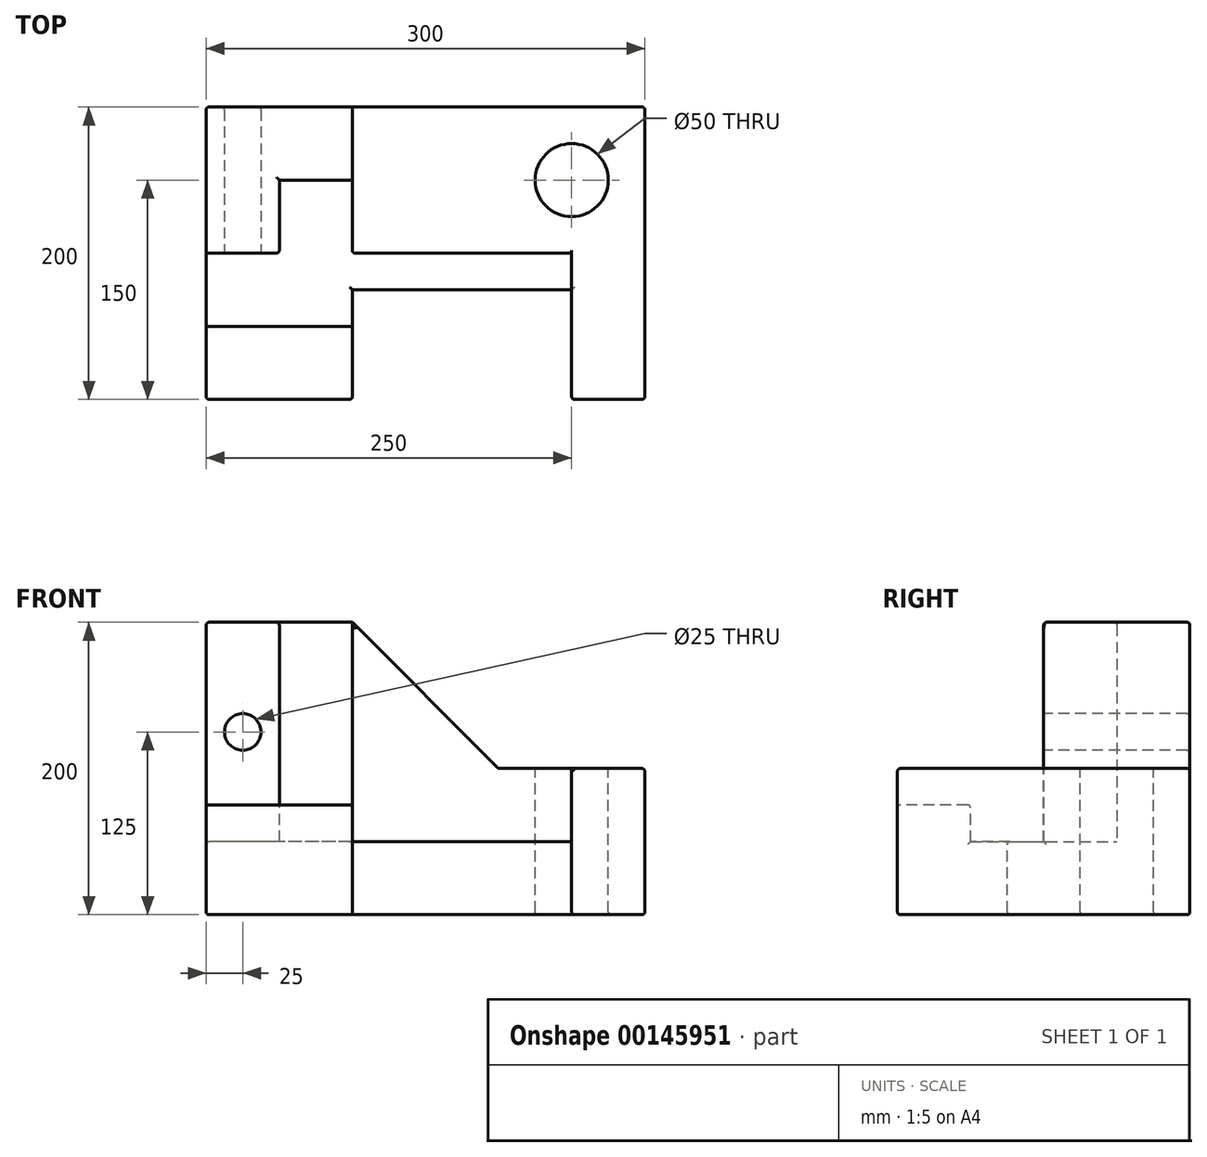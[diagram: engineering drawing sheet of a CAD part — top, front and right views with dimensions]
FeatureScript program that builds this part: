
annotation { "Feature Type Name" : "Feature", "Feature Type Description" : "" }
export const myFeature = defineFeature(function(context is Context, id is Id, definition is map)
    precondition{}
    {
        {
            var Q0;
            Q0=qCreatedBy(makeId("Front.planeOp"),FACE);
            var sketch = newSketch(context, id + "F0", { "sketchPlane" : qUnion([Q0])});
            skLineSegment(sketch, "E0", {"start": v(0, 0) * mm, "end": v(0, 200) * mm});
            skLineSegment(sketch, "E1", {"start": v(0, 200) * mm, "end": v(100, 200) * mm});
            skLineSegment(sketch, "E2", {"start": v(200, 50) * mm, "end": v(250, 50) * mm});
            skLineSegment(sketch, "E3", {"start": v(300, 50) * mm, "end": v(300, 0) * mm});
            skLineSegment(sketch, "E4", {"start": v(300, 0) * mm, "end": v(0, 0) * mm});
            skLineSegment(sketch, "E5", {"start": v(100, 200) * mm, "end": v(100, 50) * mm});
            skLineSegment(sketch, "E6", {"start": v(100, 50) * mm, "end": v(0, 50) * mm});
            skLineSegment(sketch, "E7", {"start": v(100, 50) * mm, "end": v(200, 50) * mm});
            skLineSegment(sketch, "E8", {"start": v(250, 50) * mm, "end": v(250, 0) * mm});
            skLineSegment(sketch, "E9", {"start": v(50, 50) * mm, "end": v(50, 200) * mm});
            skLineSegment(sketch, "E10", {"start": v(200, 100) * mm, "end": v(250, 100) * mm});
            skLineSegment(sketch, "E11", {"start": v(250, 50) * mm, "end": v(250, 100) * mm});
            skLineSegment(sketch, "E12", {"start": v(300, 50) * mm, "end": v(300, 100) * mm});
            skLineSegment(sketch, "E13", {"start": v(300, 100) * mm, "end": v(250, 100) * mm});
            skLineSegment(sketch, "E14", {"start": v(100, 200) * mm, "end": v(200, 100) * mm});
            skPoint(sketch, "E15.orphan", {"position": v(150, 200) * mm});
            skSolve(sketch);
        }
        {
            var Q0;
            {var subQ0=sQuery(id+"F0.wireOp",EDGE,"E5");Q0=makeQuery(id+"F0.imprint","IMPRINT",FACE,{"disambiguationData":[TD([[makeQuery(id+"F0.imprint","IMPRINT",EDGE,{"derivedFrom":subQ0}),-1.0]])]});}
            extrude(context, id + "F1", {"entities" : qUnion([Q0]), "depth" : 50 * mm});
        }
        {
            var Q0;
            {var subQ5=sQuery(id+"F0.wireOp",EDGE,"E9");Q0=makeQuery(id+"F0.imprint","IMPRINT",FACE,{"disambiguationData":[TD([[makeQuery(id+"F0.imprint","IMPRINT",EDGE,{"derivedFrom":subQ5}),1.0]])]});}
            var Q1;
            {var subQ0=sQuery(id+"F0.wireOp",EDGE,"icSDNA8W-5N0y-z0V3-qhCK-Utj477wSfauw");Q1=makeQuery(id+"F0.imprint","IMPRINT",FACE,{"disambiguationData":[TD([[makeQuery(id+"F0.imprint","IMPRINT",EDGE,{"derivedFrom":subQ0}),-1.0]])]});}
            var Q2;
            Q2=makeQuery(id+"F0.imprint","IMPRINT",FACE,{"disambiguationData":[TD([[makeQuery(id+"F0.imprint","IMPRINT",EDGE,{"derivedFrom":sQuery(id+"F0.wireOp",EDGE,"E2")}),1.0]])]});
            extrude(context, id + "F2", {"entities" : qUnion([Q0, Q1, Q2]), "operationType" : NewBodyOperationType.ADD, "depth" : 100 * mm});
        }
        {
            var Q0;
            {var subQ0=sQuery(id+"F0.wireOp",EDGE,"E7");Q0=makeQuery(id+"F0.imprint","IMPRINT",FACE,{"disambiguationData":[TD([[makeQuery(id+"F0.imprint","IMPRINT",EDGE,{"derivedFrom":subQ0}),-1.0]])]});}
            extrude(context, id + "F3", {"entities" : qUnion([Q0]), "operationType" : NewBodyOperationType.ADD, "depth" : 125 * mm});
        }
        {
            var Q0;
            {var subQ0=sQuery(id+"F0.wireOp",EDGE,"E3");Q0=makeQuery(id+"F0.imprint","IMPRINT",FACE,{"disambiguationData":[TD([[makeQuery(id+"F0.imprint","IMPRINT",EDGE,{"derivedFrom":subQ0}),-1.0]])]});}
            extrude(context, id + "F4", {"entities" : qUnion([Q0]), "operationType" : NewBodyOperationType.ADD, "depth" : 200 * mm});
        }
        {
            var Q0;
            Q0=qCreatedBy(makeId("Right.planeOp"),FACE);
            var sketch = newSketch(context, id + "F5", { "sketchPlane" : qUnion([Q0])});
            skPoint(sketch, "E16.0", {"position": v(-125, 50) * mm});
            skPoint(sketch, "E17.0", {"position": v(-125, 0) * mm});
            skLineSegment(sketch, "E18", {"start": v(-125, 50) * mm, "end": v(-150, 50) * mm});
            skLineSegment(sketch, "E19", {"start": v(-150, 50) * mm, "end": v(-150, 75) * mm});
            skLineSegment(sketch, "E20", {"start": v(-125, 0) * mm, "end": v(-125, 50) * mm});
            skLineSegment(sketch, "E21.0", {"start": v(-200, 0) * mm, "end": v(-200, 100) * mm, "construction": true});
            skLineSegment(sketch, "E22", {"start": v(-150, 75) * mm, "end": v(-200, 75) * mm});
            skLineSegment(sketch, "E23", {"start": v(-200, 75) * mm, "end": v(-200, 0) * mm});
            skLineSegment(sketch, "E24", {"start": v(-200, 0) * mm, "end": v(-125, 0) * mm});
            skSolve(sketch);
        }
        {
            var Q0;
            Q0 = qSketchRegion(id + "F5", true);
            extrude(context, id + "F6", {"entities" : qUnion([Q0]), "operationType" : NewBodyOperationType.ADD, "depth" : 100 * mm});
        }
        {
            var Q0;
            Q0=makeQuery(id+"F2.opExtrude","CAP_FACE",FACE,{"disambiguationData":[OSD([sQuery(id+"F0.wireOp",EDGE,"E0"),sQuery(id+"F0.wireOp",EDGE,"E1"),sQuery(id+"F0.wireOp",EDGE,"E6"),sQuery(id+"F0.wireOp",EDGE,"E9")])],"isStart":false});
            var sketch = newSketch(context, id + "F7", { "sketchPlane" : qUnion([Q0])});
            skCircle(sketch, "E25", {"center": v(25, 125) * mm, "radius": 12.5 * mm});
            skPoint(sketch, "E25.centerSnap0", {"position": v(25, 200) * mm});
            skSolve(sketch);
        }
        {
            var Q0;
            Q0 = qSketchRegion(id + "F7", true);
            extrude(context, id + "F8", {"entities" : qUnion([Q0]), "operationType" : NewBodyOperationType.REMOVE, "endBound" : BoundingType.THROUGH_ALL, "oppositeDirection" : true, "depth" : 25 * mm});
        }
        {
            var Q0;
            Q0=makeQuery(id+"F4.boolean.opBoolean","MERGE",FACE,{"derivedFrom":[makeQuery(id+"F2.opExtrude","SWEPT_FACE",FACE,{"disambiguationData":[OSD([sQuery(id+"F0.wireOp",EDGE,"E10")])]}),makeQuery(id+"F4.opExtrude","SWEPT_FACE",FACE,{"disambiguationData":[OSD([sQuery(id+"F0.wireOp",EDGE,"E13")])]})]});
            var sketch = newSketch(context, id + "F9", { "sketchPlane" : qUnion([Q0])});
            skCircle(sketch, "E26", {"center": v(250, -50) * mm, "radius": 25 * mm});
            skPoint(sketch, "E26.centerSnap0", {"position": v(250, 0) * mm});
            skSolve(sketch);
        }
        {
            var Q0;
            Q0 = qSketchRegion(id + "F9", true);
            extrude(context, id + "F10", {"entities" : qUnion([Q0]), "operationType" : NewBodyOperationType.REMOVE, "endBound" : BoundingType.THROUGH_ALL, "oppositeDirection" : true, "depth" : 25 * mm});
        }
        {
            var Q0;
            {var subQ0=sQuery(id+"F0.wireOp",EDGE,"E0");Q0=makeQuery(id+"F3.boolean.opBoolean","MERGE",EDGE,{"derivedFrom":[makeQuery(id+"F2.opExtrude","CAP_EDGE",EDGE,{"disambiguationData":[OSD([subQ0])],"isStart":true}),makeQuery(id+"F3.opExtrude","CAP_EDGE",EDGE,{"disambiguationData":[OSD([subQ0])],"isStart":true})]});}
            var Q1;
            Q1=makeQuery(id+"F6.boolean.opBoolean","MERGE",EDGE,{"derivedFrom":[makeQuery(id+"F3.opExtrude","SWEPT_EDGE",EDGE,{"disambiguationData":[OSD([sQuery(id+"F0.wireOp",EDGE,"E0"),sQuery(id+"F0.wireOp",EDGE,"E4")])]}),makeQuery(id+"F6.opExtrude","CAP_EDGE",EDGE,{"disambiguationData":[OSD([sQuery(id+"F5.wireOp",EDGE,"E24")])],"isStart":true})]});
            var Q2;
            Q2=makeQuery(id+"F6.boolean.opBoolean","MERGE",EDGE,{"derivedFrom":[makeQuery(id+"F3.opExtrude","SWEPT_EDGE",EDGE,{"disambiguationData":[OSD([sQuery(id+"F0.wireOp",EDGE,"E0"),sQuery(id+"F0.wireOp",EDGE,"E6")])]}),makeQuery(id+"F6.opExtrude","CAP_EDGE",EDGE,{"disambiguationData":[OSD([sQuery(id+"F5.wireOp",EDGE,"E18")])],"isStart":true})]});
            var Q3;
            Q3=makeQuery(id+"F6.opExtrude","CAP_EDGE",EDGE,{"disambiguationData":[OSD([sQuery(id+"F5.wireOp",EDGE,"E23")])],"isStart":true});
            var Q4;
            Q4=makeQuery(id+"F6.opExtrude","CAP_EDGE",EDGE,{"disambiguationData":[OSD([sQuery(id+"F5.wireOp",EDGE,"E22")])],"isStart":true});
            var Q5;
            Q5=makeQuery(id+"F6.opExtrude","CAP_EDGE",EDGE,{"disambiguationData":[OSD([sQuery(id+"F5.wireOp",EDGE,"E19")])],"isStart":true});
            var Q6;
            Q6=makeQuery(id+"F2.opExtrude","CAP_EDGE",EDGE,{"disambiguationData":[OSD([sQuery(id+"F0.wireOp",EDGE,"E0")])],"isStart":false});
            var Q7;
            Q7=makeQuery(id+"F2.opExtrude","SWEPT_EDGE",EDGE,{"disambiguationData":[OSD([sQuery(id+"F0.wireOp",EDGE,"E0"),sQuery(id+"F0.wireOp",EDGE,"E1")])]});
            var Q8;
            {var subQ0=sQuery(id+"F0.wireOp",EDGE,"E1");Q8=makeQuery(id+"F2.boolean.opBoolean","MERGE",EDGE,{"derivedFrom":[makeQuery(id+"F1.opExtrude","CAP_EDGE",EDGE,{"disambiguationData":[OSD([subQ0])],"isStart":true}),makeQuery(id+"F2.opExtrude","CAP_EDGE",EDGE,{"disambiguationData":[OSD([subQ0])],"isStart":true})]});}
            var Q9;
            Q9=makeQuery(id+"F1.opExtrude","CAP_EDGE",EDGE,{"disambiguationData":[OSD([sQuery(id+"F0.wireOp",EDGE,"E1")])],"isStart":false});
            var Q10;
            Q10=makeQuery(id+"F2.opExtrude","SWEPT_EDGE",EDGE,{"disambiguationData":[OSD([sQuery(id+"F0.wireOp",EDGE,"E1"),sQuery(id+"F0.wireOp",EDGE,"E9")])]});
            var Q11;
            Q11=makeQuery(id+"F2.opExtrude","CAP_EDGE",EDGE,{"disambiguationData":[OSD([sQuery(id+"F0.wireOp",EDGE,"E1")])],"isStart":false});
            var Q12;
            Q12=makeQuery(id+"F2.opExtrude","CAP_EDGE",EDGE,{"disambiguationData":[OSD([sQuery(id+"F0.wireOp",EDGE,"E14")])],"isStart":false});
            var Q13;
            Q13=makeQuery(id+"F2.opExtrude","CAP_EDGE",EDGE,{"disambiguationData":[OSD([sQuery(id+"F0.wireOp",EDGE,"E5")])],"isStart":false});
            var Q14;
            Q14=makeQuery(id+"F1.opExtrude","CAP_EDGE",EDGE,{"disambiguationData":[OSD([sQuery(id+"F0.wireOp",EDGE,"E6")])],"isStart":false});
            var Q15;
            Q15=makeQuery(id+"F2.opExtrude","CAP_EDGE",EDGE,{"disambiguationData":[OSD([sQuery(id+"F0.wireOp",EDGE,"E9")])],"isStart":false});
            var Q16;
            Q16=makeQuery(id+"F2.opExtrude","CAP_EDGE",EDGE,{"disambiguationData":[OSD([sQuery(id+"F0.wireOp",EDGE,"E10")])],"isStart":false});
            var Q17;
            Q17=makeQuery(id+"F2.opExtrude","CAP_EDGE",EDGE,{"disambiguationData":[OSD([sQuery(id+"F0.wireOp",EDGE,"E2"),sQuery(id+"F0.wireOp",EDGE,"E7")])],"isStart":false});
            var Q18;
            Q18=makeQuery(id+"F2.opExtrude","SWEPT_EDGE",EDGE,{"disambiguationData":[OSD([sQuery(id+"F0.wireOp",EDGE,"E10"),sQuery(id+"F0.wireOp",EDGE,"E14")])]});
            var Q19;
            Q19=makeQuery(id+"F2.opExtrude","CAP_EDGE",EDGE,{"disambiguationData":[OSD([sQuery(id+"F0.wireOp",EDGE,"E11")])],"isStart":false});
            var Q20;
            Q20=makeQuery(id+"F3.opExtrude","SWEPT_EDGE",EDGE,{"disambiguationData":[OSD([sQuery(id+"F0.wireOp",EDGE,"E2"),sQuery(id+"F0.wireOp",EDGE,"E8"),sQuery(id+"F0.wireOp",EDGE,"E11")])]});
            var Q21;
            Q21=makeQuery(id+"F3.opExtrude","CAP_EDGE",EDGE,{"disambiguationData":[OSD([sQuery(id+"F0.wireOp",EDGE,"E8")])],"isStart":false});
            var Q22;
            Q22=makeQuery(id+"F3.opExtrude","CAP_EDGE",EDGE,{"disambiguationData":[OSD([sQuery(id+"F0.wireOp",EDGE,"E2"),sQuery(id+"F0.wireOp",EDGE,"E6"),sQuery(id+"F0.wireOp",EDGE,"E7")])],"isStart":false});
            var Q23;
            Q23=makeQuery(id+"F3.opExtrude","CAP_EDGE",EDGE,{"disambiguationData":[OSD([sQuery(id+"F0.wireOp",EDGE,"E4")])],"isStart":false});
            var Q24;
            Q24=makeQuery(id+"F6.opExtrude","CAP_EDGE",EDGE,{"disambiguationData":[OSD([sQuery(id+"F5.wireOp",EDGE,"E20")])],"isStart":false});
            var Q25;
            Q25=makeQuery(id+"F6.opExtrude","CAP_EDGE",EDGE,{"disambiguationData":[OSD([sQuery(id+"F5.wireOp",EDGE,"E18")])],"isStart":false});
            var Q26;
            Q26=makeQuery(id+"F6.opExtrude","CAP_EDGE",EDGE,{"disambiguationData":[OSD([sQuery(id+"F5.wireOp",EDGE,"E19")])],"isStart":false});
            var Q27;
            Q27=makeQuery(id+"F6.opExtrude","SWEPT_EDGE",EDGE,{"disambiguationData":[OSD([sQuery(id+"F5.wireOp",EDGE,"E19"),sQuery(id+"F5.wireOp",EDGE,"E22")])]});
            var Q28;
            Q28=makeQuery(id+"F6.opExtrude","CAP_EDGE",EDGE,{"disambiguationData":[OSD([sQuery(id+"F5.wireOp",EDGE,"E22")])],"isStart":false});
            var Q29;
            Q29=makeQuery(id+"F6.opExtrude","SWEPT_EDGE",EDGE,{"disambiguationData":[OSD([sQuery(id+"F5.wireOp",EDGE,"E22"),sQuery(id+"F5.wireOp",EDGE,"E23")])]});
            var Q30;
            Q30=makeQuery(id+"F6.opExtrude","CAP_EDGE",EDGE,{"disambiguationData":[OSD([sQuery(id+"F5.wireOp",EDGE,"E23")])],"isStart":false});
            var Q31;
            Q31=makeQuery(id+"F6.opExtrude","CAP_EDGE",EDGE,{"disambiguationData":[OSD([sQuery(id+"F5.wireOp",EDGE,"E24")])],"isStart":false});
            var Q32;
            Q32=makeQuery(id+"F6.opExtrude","SWEPT_EDGE",EDGE,{"disambiguationData":[OSD([sQuery(id+"F5.wireOp",EDGE,"E23"),sQuery(id+"F5.wireOp",EDGE,"E24")])]});
            var Q33;
            Q33=makeQuery(id+"F4.opExtrude","SWEPT_EDGE",EDGE,{"disambiguationData":[OSD([sQuery(id+"F0.wireOp",EDGE,"E12"),sQuery(id+"F0.wireOp",EDGE,"E13")])]});
            var Q34;
            Q34=makeQuery(id+"F4.opExtrude","CAP_EDGE",EDGE,{"disambiguationData":[OSD([sQuery(id+"F0.wireOp",EDGE,"E13")])],"isStart":false});
            var Q35;
            Q35=makeQuery(id+"F4.opExtrude","CAP_EDGE",EDGE,{"disambiguationData":[OSD([sQuery(id+"F0.wireOp",EDGE,"E8"),sQuery(id+"F0.wireOp",EDGE,"E11")])],"isStart":false});
            var Q36;
            Q36=makeQuery(id+"F4.opExtrude","CAP_EDGE",EDGE,{"disambiguationData":[OSD([sQuery(id+"F0.wireOp",EDGE,"E3"),sQuery(id+"F0.wireOp",EDGE,"E12")])],"isStart":false});
            var Q37;
            Q37=makeQuery(id+"F4.opExtrude","CAP_EDGE",EDGE,{"disambiguationData":[OSD([sQuery(id+"F0.wireOp",EDGE,"E4")])],"isStart":false});
            var Q38;
            Q38=makeQuery(id+"F4.opExtrude","SWEPT_EDGE",EDGE,{"disambiguationData":[OSD([sQuery(id+"F0.wireOp",EDGE,"E4"),sQuery(id+"F0.wireOp",EDGE,"E8")])]});
            var Q39;
            Q39=makeQuery(id+"F4.opExtrude","SWEPT_EDGE",EDGE,{"disambiguationData":[OSD([sQuery(id+"F0.wireOp",EDGE,"E3"),sQuery(id+"F0.wireOp",EDGE,"E4")])]});
            var Q40;
            Q40=makeQuery(id+"F4.boolean.opBoolean","MERGE",EDGE,{"derivedFrom":[makeQuery(id+"F2.opExtrude","CAP_EDGE",EDGE,{"disambiguationData":[OSD([sQuery(id+"F0.wireOp",EDGE,"E10")])],"isStart":true}),makeQuery(id+"F4.opExtrude","CAP_EDGE",EDGE,{"disambiguationData":[OSD([sQuery(id+"F0.wireOp",EDGE,"E13")])],"isStart":true})]});
            var Q41;
            Q41=makeQuery(id+"F2.opExtrude","CAP_EDGE",EDGE,{"disambiguationData":[OSD([sQuery(id+"F0.wireOp",EDGE,"E14")])],"isStart":true});
            var Q42;
            Q42=makeQuery(id+"F4.opExtrude","CAP_EDGE",EDGE,{"disambiguationData":[OSD([sQuery(id+"F0.wireOp",EDGE,"E3"),sQuery(id+"F0.wireOp",EDGE,"E12")])],"isStart":true});
            var Q43;
            {var subQ0=sQuery(id+"F0.wireOp",EDGE,"E4");Q43=makeQuery(id+"F4.boolean.opBoolean","MERGE",EDGE,{"derivedFrom":[makeQuery(id+"F3.opExtrude","CAP_EDGE",EDGE,{"disambiguationData":[OSD([subQ0])],"isStart":true}),makeQuery(id+"F4.opExtrude","CAP_EDGE",EDGE,{"disambiguationData":[OSD([subQ0])],"isStart":true})]});}
            var Q44;
            Q44=makeQuery(id+"F10.boolean.opBoolean","COPY",EDGE,{"derivedFrom":makeQuery(id+"F10.opExtrude","CAP_EDGE",EDGE,{"disambiguationData":[OSD([sQuery(id+"F9.wireOp",EDGE,"E26")])],"isStart":true})});
            var Q45;
            Q45=makeQuery(id+"F8.boolean.opBoolean","COPY",EDGE,{"derivedFrom":makeQuery(id+"F8.opExtrude","CAP_EDGE",EDGE,{"disambiguationData":[OSD([sQuery(id+"F7.wireOp",EDGE,"E25")])],"isStart":true})});
            var Q46;
            {var subQ0=sQuery(id+"F0.wireOp",EDGE,"E4");Q46=makeQuery(id+"F10.boolean.opBoolean","INTERSECT",EDGE,{"derivedFrom":[makeQuery(id+"F6.boolean.opBoolean","MERGE",FACE,{"derivedFrom":[makeQuery(id+"F4.boolean.opBoolean","MERGE",FACE,{"derivedFrom":[makeQuery(id+"F3.opExtrude","SWEPT_FACE",FACE,{"disambiguationData":[OSD([subQ0])]}),makeQuery(id+"F4.opExtrude","SWEPT_FACE",FACE,{"disambiguationData":[OSD([subQ0])]})]}),makeQuery(id+"F6.opExtrude","SWEPT_FACE",FACE,{"disambiguationData":[OSD([sQuery(id+"F5.wireOp",EDGE,"E24")])]})]}),makeQuery(id+"F10.opExtrude","SWEPT_FACE",FACE,{"disambiguationData":[OSD([sQuery(id+"F9.wireOp",EDGE,"E26")])]})]});}
            var Q47;
            {var subQ0=sQuery(id+"F0.wireOp",EDGE,"E11");var subQ1=sQuery(id+"F0.wireOp",EDGE,"E8");var subQ2=sQuery(id+"F0.wireOp",EDGE,"E4");var subQ3=sQuery(id+"F0.wireOp",EDGE,"E7");var subQ4=sQuery(id+"F0.wireOp",EDGE,"E6");var subQ5=sQuery(id+"F0.wireOp",EDGE,"E2");var subQ6=sQuery(id+"F0.wireOp",EDGE,"E0");var subQ7=sQuery(id+"F0.wireOp",EDGE,"E5");var subQ8=sQuery(id+"F0.wireOp",EDGE,"E9");var subQ9=sQuery(id+"F0.wireOp",EDGE,"E1");Q47=makeQuery(id+"F8.boolean.opBoolean","INTERSECT",EDGE,{"derivedFrom":[makeQuery(id+"F4.boolean.opBoolean","MERGE",FACE,{"derivedFrom":[makeQuery(id+"F3.boolean.opBoolean","MERGE",FACE,{"derivedFrom":[makeQuery(id+"F2.boolean.opBoolean","MERGE",FACE,{"derivedFrom":[makeQuery(id+"F1.opExtrude","CAP_FACE",FACE,{"disambiguationData":[OSD([subQ9,subQ7,subQ4,subQ8])],"isStart":true}),makeQuery(id+"F2.opExtrude","CAP_FACE",FACE,{"disambiguationData":[OSD([subQ6,subQ9,subQ4,subQ8])],"isStart":true}),makeQuery(id+"F2.opExtrude","CAP_FACE",FACE,{"disambiguationData":[OSD([subQ5,subQ7,subQ3,sQuery(id+"F0.wireOp",EDGE,"E10"),subQ0,sQuery(id+"F0.wireOp",EDGE,"E14")])],"isStart":true})]}),makeQuery(id+"F3.opExtrude","CAP_FACE",FACE,{"disambiguationData":[OSD([subQ6,subQ5,subQ2,subQ4,subQ3,subQ1])],"isStart":true})]}),makeQuery(id+"F4.opExtrude","CAP_FACE",FACE,{"disambiguationData":[OSD([sQuery(id+"F0.wireOp",EDGE,"E3"),subQ2,subQ1,subQ0,sQuery(id+"F0.wireOp",EDGE,"E12"),sQuery(id+"F0.wireOp",EDGE,"E13")])],"isStart":true})]}),makeQuery(id+"F8.opExtrude","SWEPT_FACE",FACE,{"disambiguationData":[OSD([sQuery(id+"F7.wireOp",EDGE,"E25")])]})]});}
            fillet(context, id + "F11", {"entities" : qUnion([Q0, Q1, Q2, Q3, Q4, Q5, Q6, Q7, Q8, Q9, Q10, Q11, Q12, Q13, Q14, Q15, Q16, Q17, Q18, Q19, Q20, Q21, Q22, Q23, Q24, Q25, Q26, Q27, Q28, Q29, Q30, Q31, Q32, Q33, Q34, Q35, Q36, Q37, Q38, Q39, Q40, Q41, Q42, Q43, Q44, Q45, Q46, Q47]), "radius" : 1.9 * mm, "tangentPropagation" : true, "allowEdgeOverflow" : false});
        }
    });
